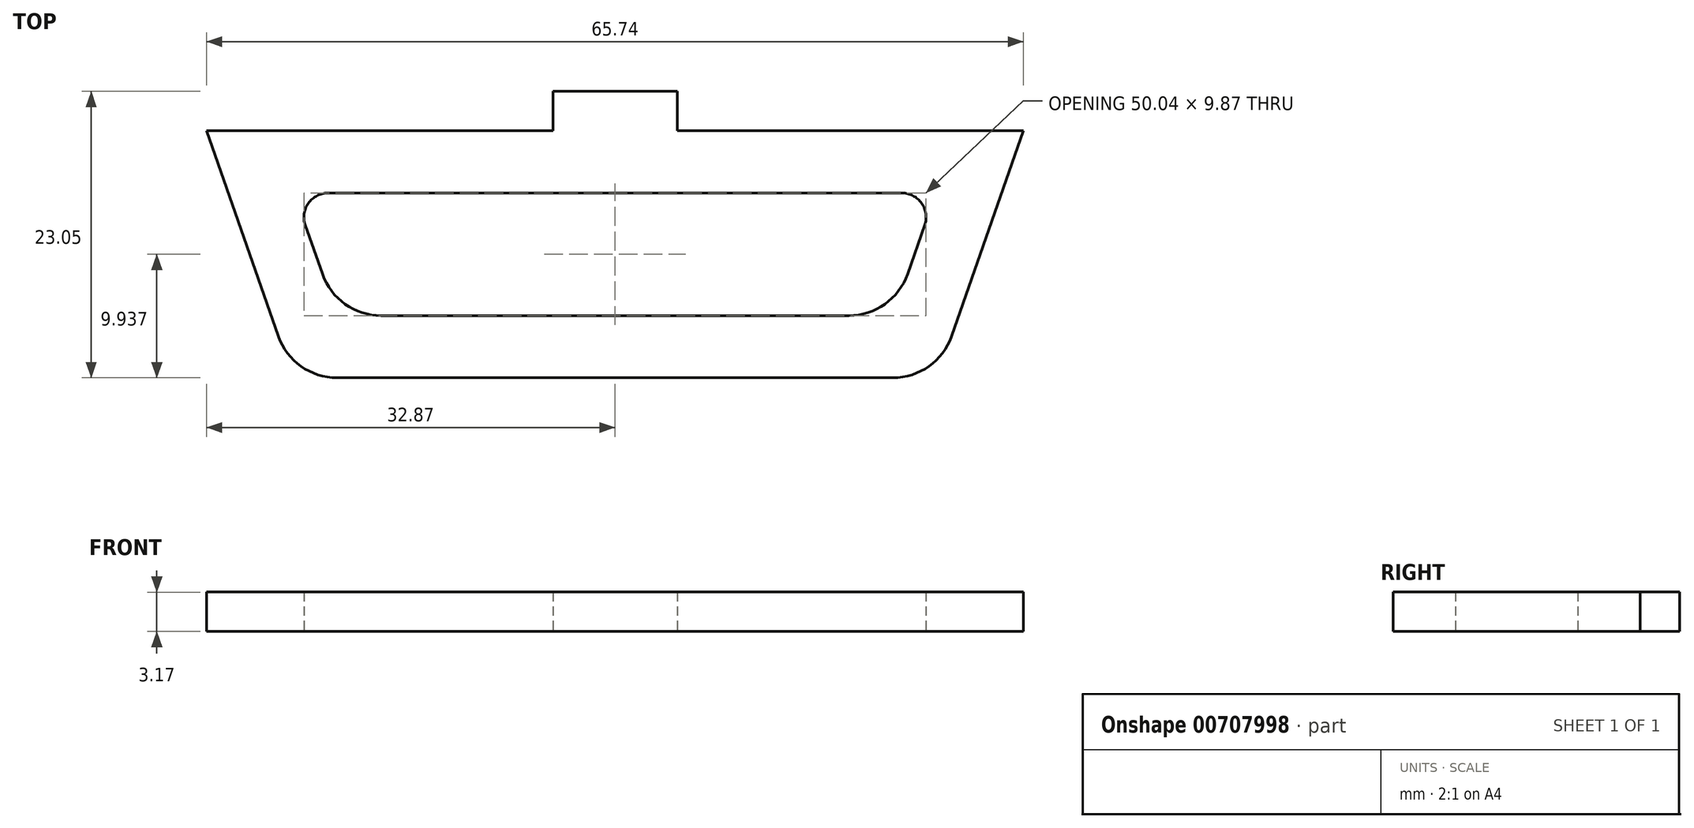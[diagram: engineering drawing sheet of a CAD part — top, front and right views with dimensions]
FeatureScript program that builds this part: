
annotation { "Feature Type Name" : "Feature", "Feature Type Description" : "" }
export const myFeature = defineFeature(function(context is Context, id is Id, definition is map)
    precondition{}
    {
        {
            var Q0;
            Q0=qCreatedBy(makeId("Top.planeOp"), FACE);
            var sketch = newSketch(context, id + "F0", { "sketchPlane" : qUnion([Q0])});
            skLineSegment(sketch, "E0", {"start": v(-35.1, -9.36) * mm, "end": v(-7.22, -9.36) * mm, "construction": true});
            skLineSegment(sketch, "E1", {"start": v(-35.1, -9.36) * mm, "end": v(-29.3, -25.88) * mm});
            skLineSegment(sketch, "E2", {"start": v(-2.22, -9.36) * mm, "end": v(-2.22, -19.03) * mm, "construction": true});
            skLineSegment(sketch, "E3.MirrorCS", {"start": v(30.65, -9.36) * mm, "end": v(24.87, -25.88) * mm});
            skLineSegment(sketch, "E4", {"start": v(-35.1, -9.36) * mm, "end": v(-7.22, -9.36) * mm});
            skLineSegment(sketch, "E5", {"start": v(-2.22, -9.36) * mm, "end": v(-2.22, -6.18) * mm, "construction": true});
            skLineSegment(sketch, "E6", {"start": v(-2.22, -6.18) * mm, "end": v(2.78, -6.18) * mm});
            skLineSegment(sketch, "E7", {"start": v(2.78, -6.18) * mm, "end": v(2.78, -9.36) * mm});
            skLineSegment(sketch, "E8.MirrorCS", {"start": v(-2.22, -6.18) * mm, "end": v(-7.22, -6.18) * mm});
            skLineSegment(sketch, "E9.MirrorCS", {"start": v(-7.22, -6.18) * mm, "end": v(-7.22, -9.36) * mm});
            skLineSegment(sketch, "E10.trimOffspring", {"start": v(2.78, -9.36) * mm, "end": v(30.65, -9.36) * mm, "construction": true});
            skLineSegment(sketch, "E11.trimOffspring", {"start": v(2.78, -9.36) * mm, "end": v(30.65, -9.36) * mm});
            skLineSegment(sketch, "E12", {"start": v(-24.6, -29.23) * mm, "end": v(20.15, -29.23) * mm});
            skPoint(sketch, "E13.visualSharp", {"position": v(-28.14, -29.23) * mm});
            skArc(sketch, "E13.filletArc", {"start": v(-29.3, -25.88) * mm, "mid": v(-27.48, -28.3) * mm, "end": v(-24.6, -29.23) * mm});
            skPoint(sketch, "E14.visualSharp", {"position": v(23.7, -29.23) * mm});
            skArc(sketch, "E14.filletArc", {"start": v(20.15, -29.23) * mm, "mid": v(23.04, -28.3) * mm, "end": v(24.87, -25.88) * mm});
            skLineSegment(sketch, "E15.0", {"start": v(2.78, -14.36) * mm, "end": v(20.87, -14.36) * mm});
            skLineSegment(sketch, "E15.1", {"start": v(22.7, -16.94) * mm, "end": v(21.32, -20.88) * mm});
            skLineSegment(sketch, "E15.2", {"start": v(-21.04, -24.23) * mm, "end": v(16.6, -24.23) * mm});
            skLineSegment(sketch, "E15.3", {"start": v(-27.14, -16.94) * mm, "end": v(-25.76, -20.88) * mm});
            skLineSegment(sketch, "E15.4", {"start": v(-25.31, -14.36) * mm, "end": v(-7.22, -14.36) * mm});
            skLineSegment(sketch, "E16", {"start": v(-7.22, -14.36) * mm, "end": v(2.78, -14.36) * mm});
            skArc(sketch, "E17.filletArc", {"start": v(-25.76, -20.88) * mm, "mid": v(-23.94, -23.3) * mm, "end": v(-21.04, -24.23) * mm});
            skArc(sketch, "E18.filletArc", {"start": v(16.6, -24.23) * mm, "mid": v(19.5, -23.3) * mm, "end": v(21.32, -20.88) * mm});
            skPoint(sketch, "E19.visualSharp", {"position": v(23.6, -14.36) * mm});
            skArc(sketch, "E19.filletArc", {"start": v(22.7, -16.94) * mm, "mid": v(22.45, -15.18) * mm, "end": v(20.87, -14.36) * mm});
            skPoint(sketch, "E20.visualSharp", {"position": v(-28.05, -14.36) * mm});
            skArc(sketch, "E20.filletArc", {"start": v(-25.31, -14.36) * mm, "mid": v(-26.9, -15.18) * mm, "end": v(-27.14, -16.94) * mm});
            skSolve(sketch);
        }
        {
            var Q0;
            Q0 = qSketchRegion(id + "F0", true);
            extrude(context, id + "F1", {"entities" : qUnion([Q0]), "depth" : 3.17 * mm, "offsetDistance" : 25 * mm});
        }
    });
